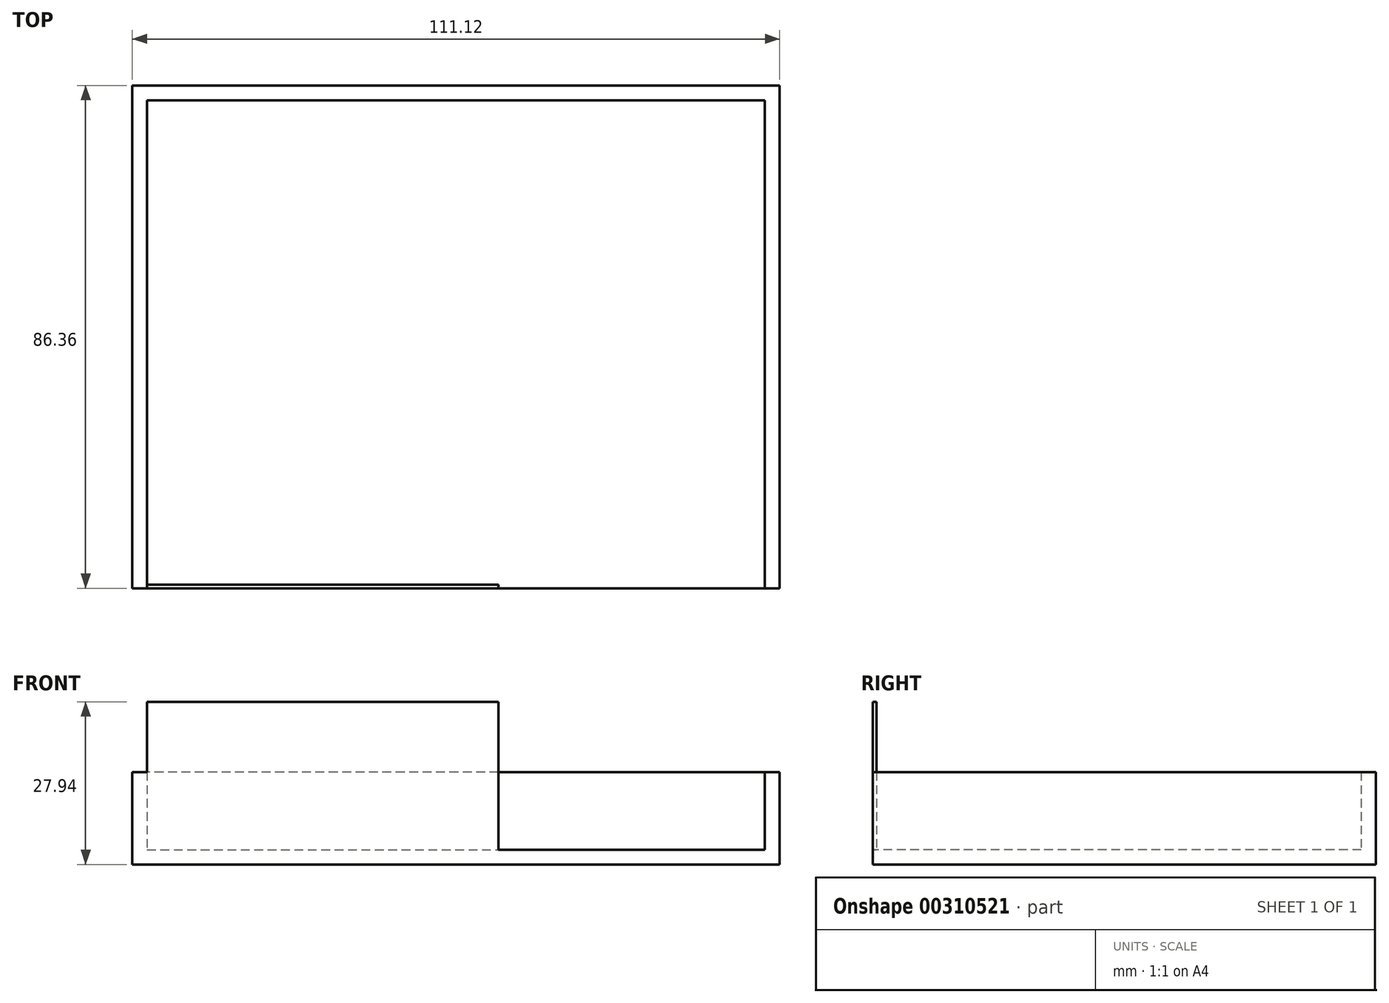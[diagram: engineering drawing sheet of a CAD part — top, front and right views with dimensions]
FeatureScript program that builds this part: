
annotation { "Feature Type Name" : "Feature", "Feature Type Description" : "" }
export const myFeature = defineFeature(function(context is Context, id is Id, definition is map)
    precondition{}
    {
        {
            var Q0;
            Q0=qCreatedBy(makeId("Top.planeOp"),FACE);
            var sketch = newSketch(context, id + "F0", { "sketchPlane" : qUnion([Q0])});
            skLineSegment(sketch, "E0.bottom", {"start": v(55.56, 43.18) * mm, "end": v(-55.56, 43.18) * mm});
            skLineSegment(sketch, "E0.top", {"start": v(55.56, -43.18) * mm, "end": v(-55.56, -43.18) * mm});
            skLineSegment(sketch, "E0.left", {"start": v(55.56, 43.18) * mm, "end": v(55.56, -43.18) * mm});
            skLineSegment(sketch, "E0.right", {"start": v(-55.56, 43.18) * mm, "end": v(-55.56, -43.18) * mm});
            skPoint(sketch, "E0.middle", {"position": v(0, 0) * mm});
            skSolve(sketch);
        }
        {
            var Q0;
            Q0=makeQuery(id+"F0.imprint","IMPRINT",FACE,{"disambiguationData":[TD([[makeQuery(id+"F0.imprint","IMPRINT",EDGE,{"derivedFrom":sQuery(id+"F0.wireOp",EDGE,"E0.bottom")}),1.0]])]});
            extrude(context, id + "F1", {"entities" : qUnion([Q0]), "depth" : 15.88 * mm});
        }
        {
            var Q0;
            Q0=makeQuery(id+"F1.opExtrude","CAP_FACE",FACE,{"disambiguationData":[OSD([sQuery(id+"F0.wireOp",EDGE,"E0.bottom"),sQuery(id+"F0.wireOp",EDGE,"E0.top"),sQuery(id+"F0.wireOp",EDGE,"E0.left"),sQuery(id+"F0.wireOp",EDGE,"E0.right")])],"isStart":false});
            var Q1;
            Q1=makeQuery(id+"F1.opExtrude","SWEPT_FACE",FACE,{"disambiguationData":[OSD([sQuery(id+"F0.wireOp",EDGE,"E0.top")])]});
            shell(context, id + "F2", {"entities" : qUnion([Q0, Q1]), "thickness" : 2.54 * mm});
        }
        {
            var Q0;
            Q0=makeQuery(id+"F2.opShell","OFFSET_FACE",FACE,{"disambiguationData":[OSD([sQuery(id+"F0.wireOp",EDGE,"E0.bottom"),sQuery(id+"F0.wireOp",EDGE,"E0.top"),sQuery(id+"F0.wireOp",EDGE,"E0.left"),sQuery(id+"F0.wireOp",EDGE,"E0.right")])]});
            var sketch = newSketch(context, id + "F3", { "sketchPlane" : qUnion([Q0])});
            skLineSegment(sketch, "E1.bottom", {"start": v(-53.02, -43.18) * mm, "end": v(7.3, -43.18) * mm});
            skLineSegment(sketch, "E1.top", {"start": v(-53.02, -42.55) * mm, "end": v(7.3, -42.55) * mm});
            skLineSegment(sketch, "E1.left", {"start": v(-53.02, -43.18) * mm, "end": v(-53.02, -42.55) * mm});
            skLineSegment(sketch, "E1.right", {"start": v(7.3, -43.18) * mm, "end": v(7.3, -42.55) * mm});
            skSolve(sketch);
        }
        {
            var Q0;
            Q0=makeQuery(id+"F3.imprint","IMPRINT",FACE,{"disambiguationData":[TD([[makeQuery(id+"F3.imprint","IMPRINT",EDGE,{"derivedFrom":sQuery(id+"F3.wireOp",EDGE,"E1.bottom")}),-1.0]])]});
            extrude(context, id + "F4", {"entities" : qUnion([Q0]), "operationType" : NewBodyOperationType.ADD, "depth" : 25.4 * mm});
        }
    });
